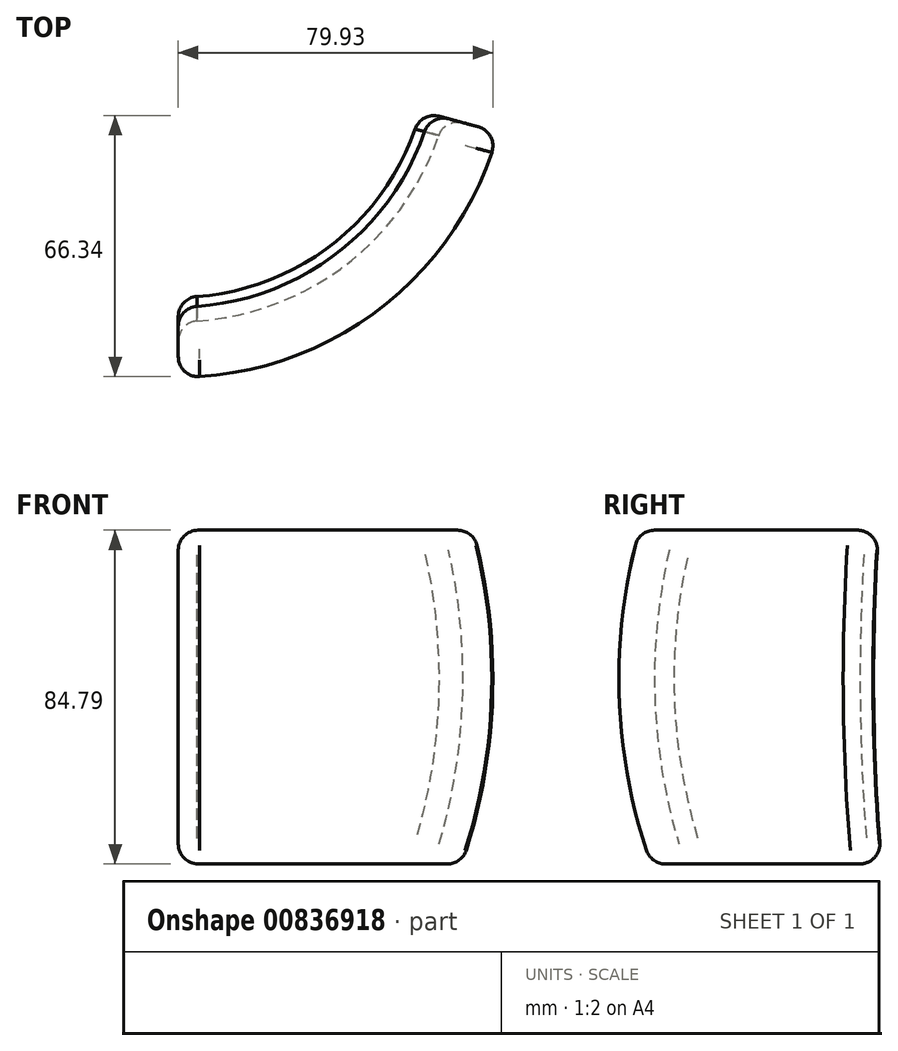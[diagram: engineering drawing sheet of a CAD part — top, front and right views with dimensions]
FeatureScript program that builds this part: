
annotation { "Feature Type Name" : "Feature", "Feature Type Description" : "" }
export const myFeature = defineFeature(function(context is Context, id is Id, definition is map)
    precondition{}
    {
        {
            var Q0;
            Q0=qCreatedBy(makeId("Right.planeOp"),FACE);
            var sketch = newSketch(context, id + "F0", { "sketchPlane" : qUnion([Q0])});
            skLineSegment(sketch, "E0", {"start": v(0, 0) * mm, "end": v(0, 46.33) * mm, "construction": true});
            skArc(sketch, "E1", {"start": v(-64.77, 37.73) * mm, "mid": v(-69.88, -4.9) * mm, "end": v(-61.8, -47.06) * mm});
            skArc(sketch, "E2", {"start": v(-78.9, 37.73) * mm, "mid": v(-84, -4.9) * mm, "end": v(-75.92, -47.06) * mm});
            skLineSegment(sketch, "E3", {"start": v(-78.9, 37.73) * mm, "end": v(-64.77, 37.73) * mm});
            skLineSegment(sketch, "E4", {"start": v(-75.92, -47.06) * mm, "end": v(-61.8, -47.06) * mm});
            skSolve(sketch);
        }
        {
            var Q0;
            Q0=makeQuery(id+"F0.imprint","IMPRINT",FACE,{"disambiguationData":[TD([[makeQuery(id+"F0.imprint","IMPRINT",EDGE,{"derivedFrom":sQuery(id+"F0.wireOp",EDGE,"E1")}),-1.0]])]});
            var Q1;
            Q1=sQuery(id+"F0.wireOp",EDGE,"E0");
            revolve(context, id + "F1", {"surfaceOperationType" : NewSurfaceOperationType.NEW, "entities" : qUnion([Q0]), "axis" : qUnion([Q1]), "revolveType" : RevolveType.ONE_DIRECTION, "angle" : 75 * degree});
        }
        {
            var Q0;
            Q0=makeQuery(id+"F1.opRevolve","SWEPT_EDGE",EDGE,{"disambiguationData":[OSD([sQuery(id+"F0.wireOp",EDGE,"E2"),sQuery(id+"F0.wireOp",EDGE,"E3")])]});
            var Q1;
            Q1=makeQuery(id+"F1.opRevolve","SWEPT_EDGE",EDGE,{"disambiguationData":[OSD([sQuery(id+"F0.wireOp",EDGE,"E2"),sQuery(id+"F0.wireOp",EDGE,"E4")])]});
            var Q2;
            Q2=makeQuery(id+"F1.opRevolve","CAP_EDGE",EDGE,{"disambiguationData":[OSD([sQuery(id+"F0.wireOp",EDGE,"E3")])],"isStart":false});
            var Q3;
            Q3=makeQuery(id+"F1.opRevolve","CAP_EDGE",EDGE,{"disambiguationData":[OSD([sQuery(id+"F0.wireOp",EDGE,"E4")])],"isStart":false});
            var Q4;
            Q4=makeQuery(id+"F1.opRevolve","CAP_EDGE",EDGE,{"disambiguationData":[OSD([sQuery(id+"F0.wireOp",EDGE,"E2")])],"isStart":false});
            var Q5;
            Q5=makeQuery(id+"F1.opRevolve","CAP_EDGE",EDGE,{"disambiguationData":[OSD([sQuery(id+"F0.wireOp",EDGE,"E2")])],"isStart":true});
            var Q6;
            Q6=makeQuery(id+"F1.opRevolve","CAP_EDGE",EDGE,{"disambiguationData":[OSD([sQuery(id+"F0.wireOp",EDGE,"E3")])],"isStart":true});
            var Q7;
            Q7=makeQuery(id+"F1.opRevolve","CAP_EDGE",EDGE,{"disambiguationData":[OSD([sQuery(id+"F0.wireOp",EDGE,"E4")])],"isStart":true});
            var Q8;
            Q8=makeQuery(id+"F1.opRevolve","CAP_EDGE",EDGE,{"disambiguationData":[OSD([sQuery(id+"F0.wireOp",EDGE,"E1")])],"isStart":false});
            var Q9;
            Q9=makeQuery(id+"F1.opRevolve","SWEPT_EDGE",EDGE,{"disambiguationData":[OSD([sQuery(id+"F0.wireOp",EDGE,"E1"),sQuery(id+"F0.wireOp",EDGE,"E3")])]});
            var Q10;
            Q10=makeQuery(id+"F1.opRevolve","SWEPT_EDGE",EDGE,{"disambiguationData":[OSD([sQuery(id+"F0.wireOp",EDGE,"E1"),sQuery(id+"F0.wireOp",EDGE,"E4")])]});
            var Q11;
            Q11=makeQuery(id+"F1.opRevolve","CAP_EDGE",EDGE,{"disambiguationData":[OSD([sQuery(id+"F0.wireOp",EDGE,"E1")])],"isStart":true});
            fillet(context, id + "F2", {"entities" : qUnion([Q0, Q1, Q2, Q3, Q4, Q5, Q6, Q7, Q8, Q9, Q10, Q11]), "radius" : 5.08 * mm, "tangentPropagation" : true, "allowEdgeOverflow" : false});
        }
    });
